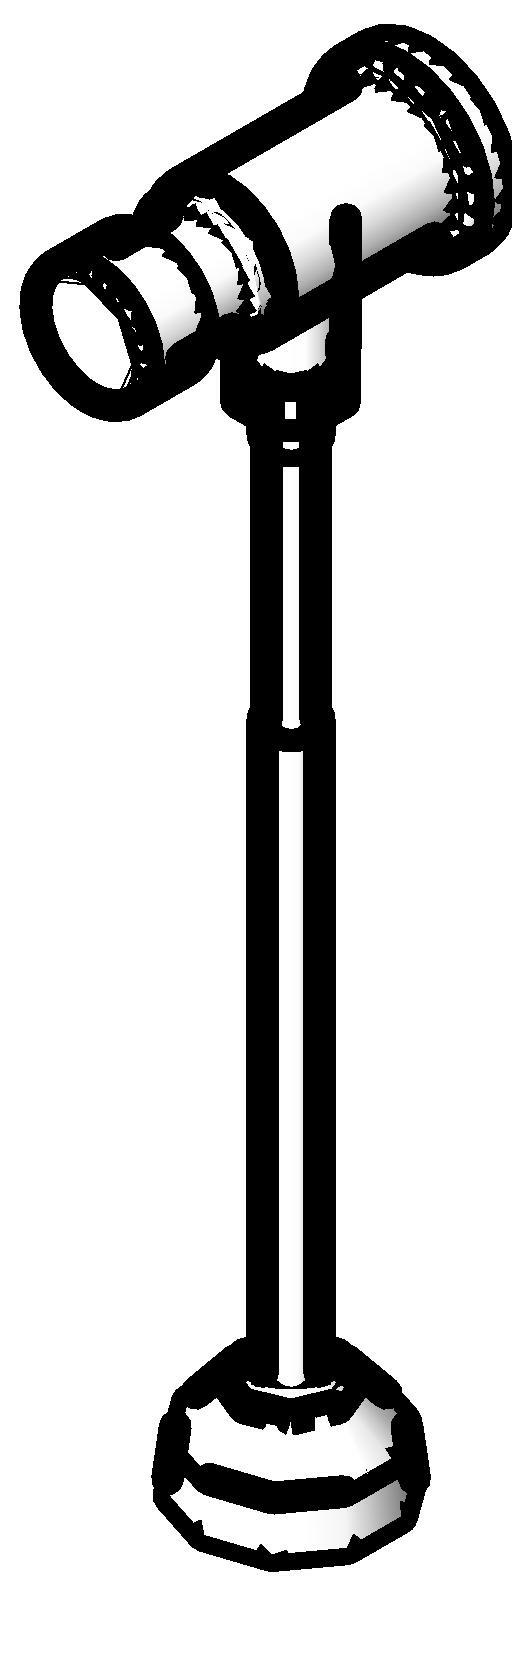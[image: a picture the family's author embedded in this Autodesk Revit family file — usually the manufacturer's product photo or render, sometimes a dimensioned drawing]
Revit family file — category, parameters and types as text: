
# Revit family: Deca_Valvula para mictorio horizontal_Decamatic Eco_2572
name_source: partatom
category: Plumbing Fixtures
units: mm (PartAtom-declared; Revit-internal decimal feet)

## family parameters
Cut with Voids When Loaded = No
Host = Face
Part Type = Normal
Room Calculation Point = No
Round Connector Dimension = Use Radius
Shared = No

## types (1)
- 2572.C_Cromado_DN15
    Acompanha o Produto = Acompanha Flexivel
    Aprovado por = quattroD
    Atendimento ao Cliente = 0800-0117073
    CWFU = 0
    Categoria = SISTEMAS DE DESCARGA
    Composição Anel Vedação = -
    Composição Assento = -
    Composição Básica = Liga de Cobre (bronze e latão),Plásticos de Engenharia,Elastômeros
    Composição Componente = -
    Consumo = 8 l/min
    Cor Interna = -
    Cor Principal = Cromado
    Cor Secundária = -
    Cores Componente = -
    Criado por = quattroD
    Código Pai = 2572
    Default Elevation = 1100 mm
    Description = Válvula de mictório horizontal com fechamento automático
    Diâmetro Água Fria = 15 mm  [stored 0.0492126 ft]
    Diâmetro Água Fria Saída = 15 mm  [stored 0.0492126 ft]
    HWFU = 0
    Informações Complementares = -
    Itens de Instalação = -
    Linha = Decamatic Eco
    Manufacturer = Deca
    Material = Deca_Cromado
    Model = 2572.C
    Norma = NBR13713
    Peso Líquido (Kg) = 0.66
    Pressão máx. funcionamento = 40 MCA
    Pressão mín. Aquec. Acúmulo = -
    Pressão mín. Aquec. Passagem = -
    Pressão mín. funcionamento = 2 MCA
    Raio Água Fria = 8 mm  [stored 0.0262467 ft]
    Raio Água Fria Saída = 8 mm  [stored 0.0262467 ft]
    Saída de Esgoto = -
    Segmento = Banheiro Competitivo
    Tipo de dispositivo economizador = Sim
    Tipo de mecanismo utilizado = -
    Tipo de rosca de entrada = BSP NBR 8133
    Tipo de rosca de saída = BSP NBR 8133
    URL = www.deca.com.br
    Vazão na Pressão máx. (L/min) = 8
    Vazão na Pressão mín. (L/min) = 5

note: source unit labels omitted for Vazão na Pressão máx. (L/min), Vazão na Pressão mín. (L/min) — the stored unit's dimension contradicts the parameter name (converter mislabeling)

note: [stored X ft] marks values corroborated as IEEE doubles in the binary element streams (Revit-internal decimal feet)

## geometry (parser evidence)
native form markers: Sweep x1
no freeform markers — native parametric forms only
